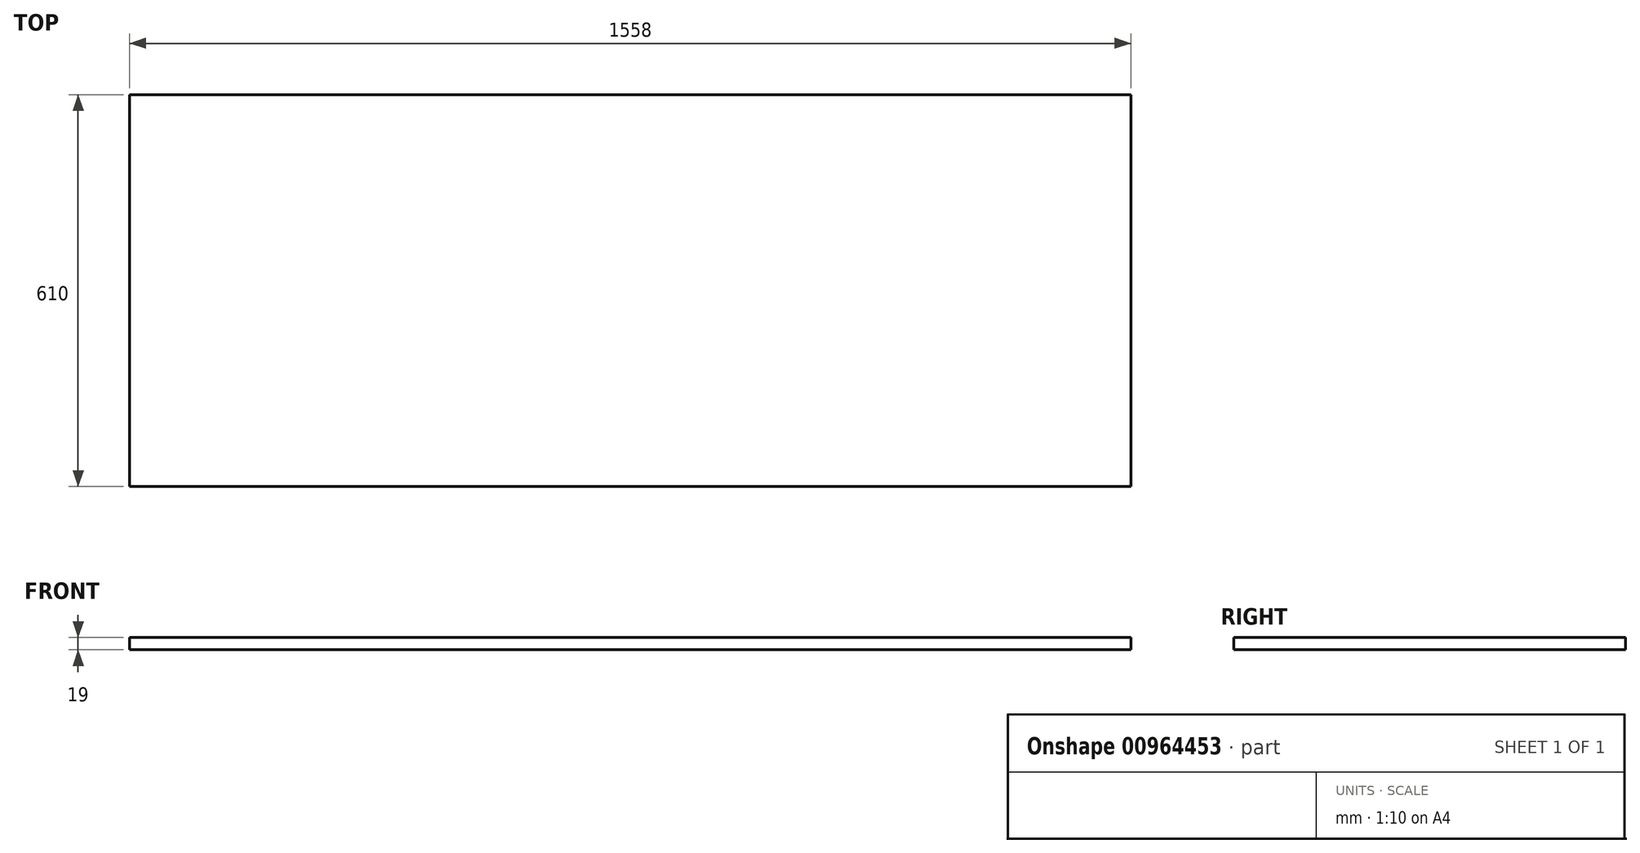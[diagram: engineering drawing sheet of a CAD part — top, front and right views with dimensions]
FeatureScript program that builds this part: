
annotation { "Feature Type Name" : "Feature", "Feature Type Description" : "" }
export const myFeature = defineFeature(function(context is Context, id is Id, definition is map)
    precondition{}
    {
        {
            var Q0;
            Q0=qCreatedBy(makeId("Top.planeOp"),FACE);
            var sketch = newSketch(context, id + "F0", { "sketchPlane" : qUnion([Q0])});
            skLineSegment(sketch, "E0.bottom", {"start": v(0, 0) * mm, "end": v(1558, 0) * mm});
            skLineSegment(sketch, "E0.top", {"start": v(0, 610) * mm, "end": v(1558, 610) * mm});
            skLineSegment(sketch, "E0.left", {"start": v(0, 0) * mm, "end": v(0, 610) * mm});
            skLineSegment(sketch, "E0.right", {"start": v(1558, 0) * mm, "end": v(1558, 610) * mm});
            skSolve(sketch);
        }
        {
            var Q0;
            Q0=qSketchRegion(id+"F0",true);
            extrude(context, id + "F1", {"entities" : qUnion([Q0]), "depth" : 19 * mm, "offsetDistance" : 25 * mm});
        }
    });
